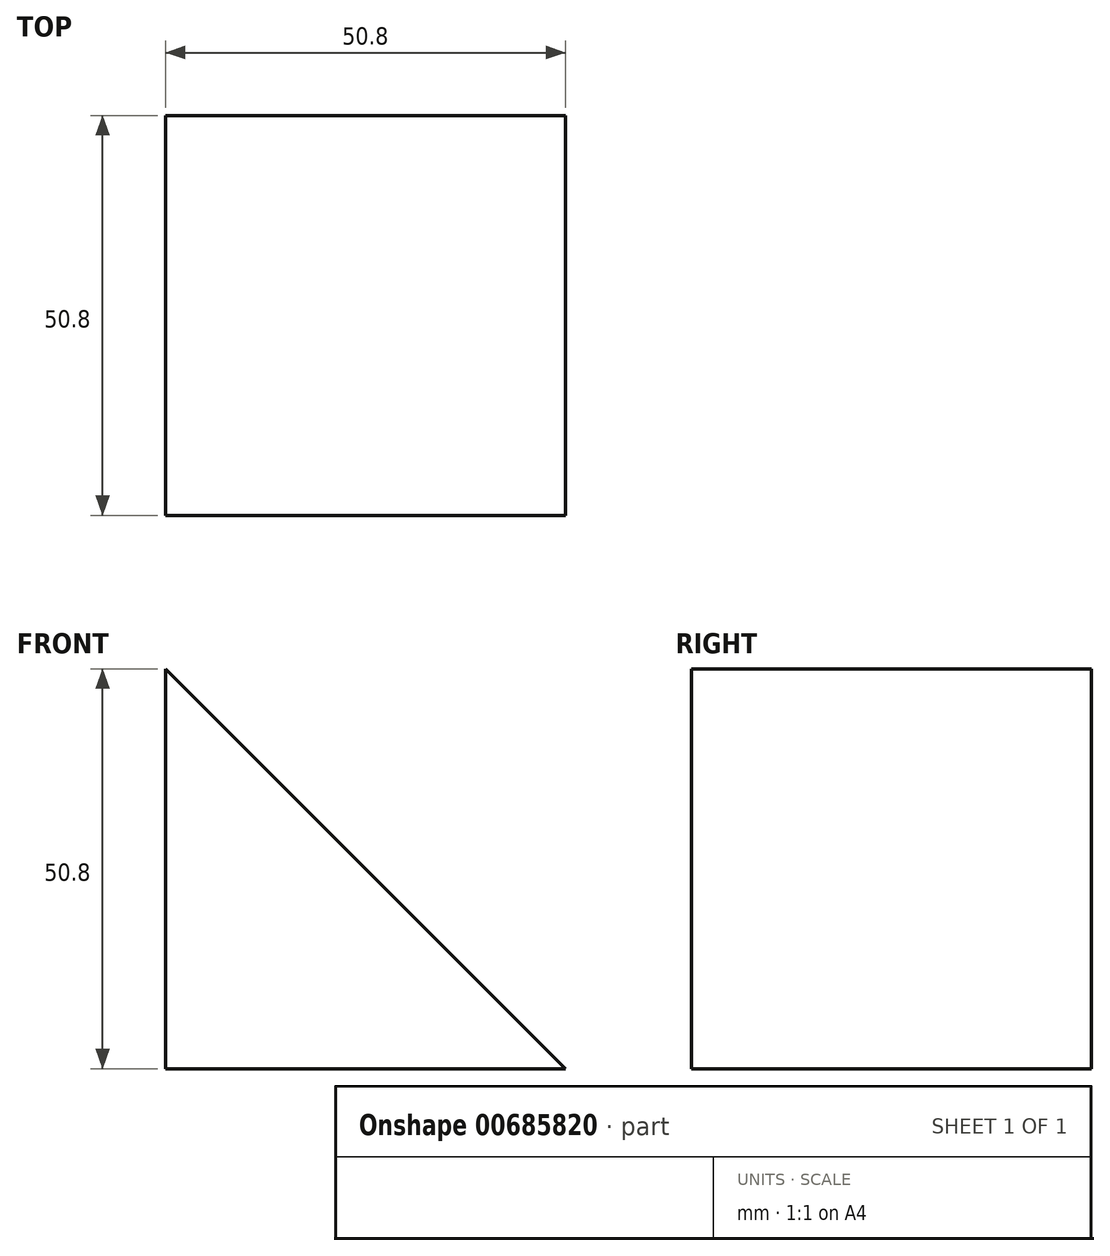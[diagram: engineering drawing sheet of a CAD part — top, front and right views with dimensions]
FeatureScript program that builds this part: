
annotation { "Feature Type Name" : "Feature", "Feature Type Description" : "" }
export const myFeature = defineFeature(function(context is Context, id is Id, definition is map)
    precondition{}
    {
        {
            var Q0;
            Q0=qCreatedBy(makeId("Front.planeOp"),FACE);
            var sketch = newSketch(context, id + "F0", { "sketchPlane" : qUnion([Q0])});
            skLineSegment(sketch, "E0", {"start": v(-53.18, 23.2) * mm, "end": v(-53.18, -27.6) * mm});
            skLineSegment(sketch, "E1", {"start": v(-53.18, -27.6) * mm, "end": v(-2.38, -27.6) * mm});
            skLineSegment(sketch, "E2", {"start": v(-53.18, 23.2) * mm, "end": v(-2.38, -27.6) * mm});
            skSolve(sketch);
        }
        {
            var Q0;
            Q0 = qSketchRegion(id + "F0", true);
            extrude(context, id + "F1", {"entities" : qUnion([Q0]), "depth" : 50.8 * mm, "offsetDistance" : 25.4 * mm});
        }
    });
